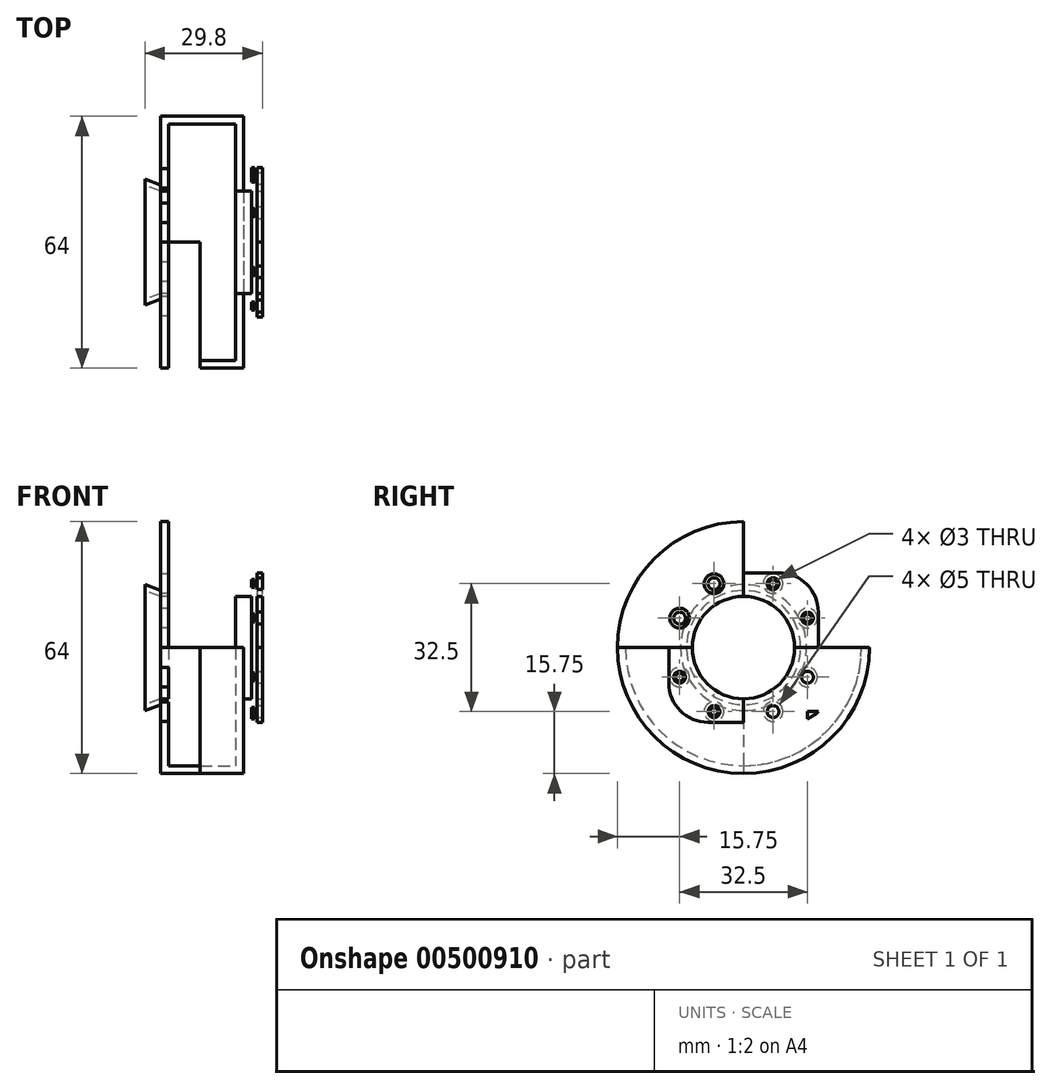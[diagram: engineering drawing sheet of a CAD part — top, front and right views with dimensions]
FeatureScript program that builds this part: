
annotation { "Feature Type Name" : "Feature", "Feature Type Description" : "" }
export const myFeature = defineFeature(function(context is Context, id is Id, definition is map)
    precondition{}
    {
        {
            var Q0;
            Q0=qCreatedBy(makeId("Right.planeOp"),FACE);
            var sketch = newSketch(context, id + "F0", { "sketchPlane" : qUnion([Q0])});
            skLineSegment(sketch, "E0.bottom", {"start": v(19, 19) * mm, "end": v(-19, 19) * mm});
            skLineSegment(sketch, "E0.top", {"start": v(19, -19) * mm, "end": v(-19, -19) * mm});
            skLineSegment(sketch, "E0.left", {"start": v(19, 19) * mm, "end": v(19, -19) * mm});
            skLineSegment(sketch, "E0.right", {"start": v(-19, 19) * mm, "end": v(-19, -19) * mm});
            skPoint(sketch, "E0.middle", {"position": v(0, 0) * mm});
            skCircle(sketch, "E1", {"center": v(0, 0) * mm, "radius": 13 * mm});
            skSolve(sketch);
        }
        {
            var Q0;
            Q0=makeQuery(id+"F0.imprint","IMPRINT",FACE,{"disambiguationData":[TD([[makeQuery(id+"F0.imprint","IMPRINT",EDGE,{"derivedFrom":sQuery(id+"F0.wireOp",EDGE,"E0.bottom")}),1.0]])]});
            extrude(context, id + "F1", {"entities" : qUnion([Q0]), "depth" : 2.8 * mm});
        }
        {
            var Q0;
            Q0=makeQuery(id+"F1.opExtrude","CAP_FACE",FACE,{"disambiguationData":[OSD([sQuery(id+"F0.wireOp",EDGE,"E0.bottom"),sQuery(id+"F0.wireOp",EDGE,"E0.top"),sQuery(id+"F0.wireOp",EDGE,"E0.left"),sQuery(id+"F0.wireOp",EDGE,"E0.right"),sQuery(id+"F0.wireOp",EDGE,"E1")])],"isStart":false});
            var sketch = newSketch(context, id + "F2", { "sketchPlane" : qUnion([Q0])});
            skLineSegment(sketch, "E2", {"start": v(-19, -19) * mm, "end": v(-16.25, -19) * mm});
            skLineSegment(sketch, "E3", {"start": v(-16.25, -19) * mm, "end": v(-16.25, -7.5) * mm});
            skCircle(sketch, "E4", {"center": v(-16.25, -7.5) * mm, "radius": 1.5 * mm});
            skLineSegment(sketch, "E5", {"start": v(-32.62, 0) * mm, "end": v(36.48, 0) * mm});
            skLineSegment(sketch, "E6", {"start": v(0, -24.37) * mm, "end": v(0, 22.32) * mm});
            skPoint(sketch, "E6.endSnap0", {"position": v(0, 19) * mm});
            skCircle(sketch, "E7.MirrorC", {"center": v(16.25, -7.5) * mm, "radius": 1.5 * mm});
            skCircle(sketch, "E8.MirrorC", {"center": v(-16.25, 7.5) * mm, "radius": 1.5 * mm});
            skCircle(sketch, "E9.MirrorC", {"center": v(16.25, 7.5) * mm, "radius": 1.5 * mm});
            skLineSegment(sketch, "E10", {"start": v(-19, -19) * mm, "end": v(-19, -16.25) * mm});
            skLineSegment(sketch, "E11", {"start": v(-19, -16.25) * mm, "end": v(-7.5, -16.25) * mm});
            skCircle(sketch, "E12", {"center": v(-7.5, -16.25) * mm, "radius": 1.5 * mm});
            skCircle(sketch, "E13.MirrorC", {"center": v(7.5, -16.25) * mm, "radius": 1.5 * mm});
            skCircle(sketch, "E14.MirrorC", {"center": v(-7.5, 16.25) * mm, "radius": 1.5 * mm});
            skCircle(sketch, "E15.MirrorC", {"center": v(7.5, 16.25) * mm, "radius": 1.5 * mm});
            skSolve(sketch);
        }
        {
            var Q0;
            Q0=makeQuery(id+"F2.imprint","IMPRINT",FACE,{"disambiguationData":[TD([[makeQuery(id+"F2.imprint","IMPRINT",EDGE,{"derivedFrom":sQuery(id+"F2.wireOp",EDGE,"E7.MirrorC")}),-1.0]])]});
            var Q1;
            Q1=makeQuery(id+"F2.imprint","IMPRINT",FACE,{"disambiguationData":[TD([[makeQuery(id+"F2.imprint","IMPRINT",EDGE,{"derivedFrom":sQuery(id+"F2.wireOp",EDGE,"E4")}),1.0]])]});
            var Q2;
            Q2=makeQuery(id+"F2.imprint","IMPRINT",FACE,{"disambiguationData":[TD([[makeQuery(id+"F2.imprint","IMPRINT",EDGE,{"derivedFrom":sQuery(id+"F2.wireOp",EDGE,"E9.MirrorC")}),1.0]])]});
            var Q3;
            Q3=makeQuery(id+"F2.imprint","IMPRINT",FACE,{"disambiguationData":[TD([[makeQuery(id+"F2.imprint","IMPRINT",EDGE,{"derivedFrom":sQuery(id+"F2.wireOp",EDGE,"E12")}),1.0]])]});
            var Q4;
            Q4=makeQuery(id+"F2.imprint","IMPRINT",FACE,{"disambiguationData":[TD([[makeQuery(id+"F2.imprint","IMPRINT",EDGE,{"derivedFrom":sQuery(id+"F2.wireOp",EDGE,"E13.MirrorC")}),-1.0]])]});
            var Q5;
            Q5=makeQuery(id+"F2.imprint","IMPRINT",FACE,{"disambiguationData":[TD([[makeQuery(id+"F2.imprint","IMPRINT",EDGE,{"derivedFrom":sQuery(id+"F2.wireOp",EDGE,"E15.MirrorC")}),1.0]])]});
            var Q6;
            Q6=makeQuery(id+"F2.imprint","IMPRINT",FACE,{"disambiguationData":[TD([[makeQuery(id+"F2.imprint","IMPRINT",EDGE,{"derivedFrom":sQuery(id+"F2.wireOp",EDGE,"E8.MirrorC")}),-1.0]])]});
            var Q7;
            Q7=makeQuery(id+"F2.imprint","IMPRINT",FACE,{"disambiguationData":[TD([[makeQuery(id+"F2.imprint","IMPRINT",EDGE,{"derivedFrom":sQuery(id+"F2.wireOp",EDGE,"E14.MirrorC")}),-1.0]])]});
            extrude(context, id + "F3", {"entities" : qUnion([Q0, Q1, Q2, Q3, Q4, Q5, Q6, Q7]), "operationType" : NewBodyOperationType.REMOVE, "oppositeDirection" : true, "depth" : 2 * mm});
        }
        {
            var Q0;
            Q0=makeQuery(id+"F1.opExtrude","CAP_FACE",FACE,{"disambiguationData":[OSD([sQuery(id+"F0.wireOp",EDGE,"E0.bottom"),sQuery(id+"F0.wireOp",EDGE,"E0.top"),sQuery(id+"F0.wireOp",EDGE,"E0.left"),sQuery(id+"F0.wireOp",EDGE,"E0.right"),sQuery(id+"F0.wireOp",EDGE,"E1")])],"isStart":true});
            var sketch = newSketch(context, id + "F4", { "sketchPlane" : qUnion([Q0])});
            skLineSegment(sketch, "E16", {"start": v(-19, -19) * mm, "end": v(-16.25, -19) * mm});
            skLineSegment(sketch, "E17", {"start": v(-16.25, -19) * mm, "end": v(-16.25, -7.5) * mm});
            skLineSegment(sketch, "E18", {"start": v(-19, -19) * mm, "end": v(-19, -16.25) * mm});
            skLineSegment(sketch, "E19", {"start": v(-19, -16.25) * mm, "end": v(-7.5, -16.25) * mm});
            skCircle(sketch, "E20", {"center": v(-16.25, -7.5) * mm, "radius": 1 * mm});
            skCircle(sketch, "E21", {"center": v(-7.5, -16.25) * mm, "radius": 1 * mm});
            skCircle(sketch, "E22.MirrorC", {"center": v(-16.25, 7.5) * mm, "radius": 1 * mm});
            skCircle(sketch, "E23.MirrorC", {"center": v(-7.5, 16.25) * mm, "radius": 1 * mm});
            skCircle(sketch, "E24.MirrorC", {"center": v(7.5, 16.25) * mm, "radius": 1 * mm});
            skCircle(sketch, "E25.MirrorC", {"center": v(7.5, -16.25) * mm, "radius": 1 * mm});
            skCircle(sketch, "E26.MirrorC", {"center": v(16.25, -7.5) * mm, "radius": 1 * mm});
            skCircle(sketch, "E27.MirrorC", {"center": v(16.25, 7.5) * mm, "radius": 1 * mm});
            skSolve(sketch);
        }
        {
            var Q0;
            Q0=makeQuery(id+"F4.imprint","IMPRINT",FACE,{"disambiguationData":[TD([[makeQuery(id+"F4.imprint","IMPRINT",EDGE,{"derivedFrom":sQuery(id+"F4.wireOp",EDGE,"E20")}),1.0]])]});
            var Q1;
            Q1=makeQuery(id+"F4.imprint","IMPRINT",FACE,{"disambiguationData":[TD([[makeQuery(id+"F4.imprint","IMPRINT",EDGE,{"derivedFrom":sQuery(id+"F4.wireOp",EDGE,"E21")}),1.0]])]});
            var Q2;
            Q2=makeQuery(id+"F4.imprint","IMPRINT",FACE,{"disambiguationData":[TD([[makeQuery(id+"F4.imprint","IMPRINT",EDGE,{"derivedFrom":sQuery(id+"F4.wireOp",EDGE,"E22.MirrorC")}),-1.0]])]});
            var Q3;
            Q3=makeQuery(id+"F4.imprint","IMPRINT",FACE,{"disambiguationData":[TD([[makeQuery(id+"F4.imprint","IMPRINT",EDGE,{"derivedFrom":sQuery(id+"F4.wireOp",EDGE,"E23.MirrorC")}),-1.0]])]});
            var Q4;
            Q4=makeQuery(id+"F4.imprint","IMPRINT",FACE,{"disambiguationData":[TD([[makeQuery(id+"F4.imprint","IMPRINT",EDGE,{"derivedFrom":sQuery(id+"F4.wireOp",EDGE,"E24.MirrorC")}),1.0]])]});
            var Q5;
            Q5=makeQuery(id+"F4.imprint","IMPRINT",FACE,{"disambiguationData":[TD([[makeQuery(id+"F4.imprint","IMPRINT",EDGE,{"derivedFrom":sQuery(id+"F4.wireOp",EDGE,"E25.MirrorC")}),-1.0]])]});
            var Q6;
            Q6=makeQuery(id+"F4.imprint","IMPRINT",FACE,{"disambiguationData":[TD([[makeQuery(id+"F4.imprint","IMPRINT",EDGE,{"derivedFrom":sQuery(id+"F4.wireOp",EDGE,"E26.MirrorC")}),-1.0]])]});
            var Q7;
            Q7=makeQuery(id+"F4.imprint","IMPRINT",FACE,{"disambiguationData":[TD([[makeQuery(id+"F4.imprint","IMPRINT",EDGE,{"derivedFrom":sQuery(id+"F4.wireOp",EDGE,"E27.MirrorC")}),1.0]])]});
            extrude(context, id + "F5", {"entities" : qUnion([Q0, Q1, Q2, Q3, Q4, Q5, Q6, Q7]), "operationType" : NewBodyOperationType.REMOVE, "oppositeDirection" : true, "depth" : 1.5 * mm});
        }
        {
            var Q0;
            Q0=makeQuery(id+"F1.opExtrude","CAP_FACE",FACE,{"disambiguationData":[OSD([sQuery(id+"F0.wireOp",EDGE,"E0.bottom"),sQuery(id+"F0.wireOp",EDGE,"E0.top"),sQuery(id+"F0.wireOp",EDGE,"E0.left"),sQuery(id+"F0.wireOp",EDGE,"E0.right"),sQuery(id+"F0.wireOp",EDGE,"E1")])],"isStart":true});
            var sketch = newSketch(context, id + "F6", { "sketchPlane" : qUnion([Q0])});
            skCircle(sketch, "E28", {"center": v(0, 0) * mm, "radius": 13 * mm});
            skCircle(sketch, "E29", {"center": v(0, 0) * mm, "radius": 14.5 * mm});
            skSolve(sketch);
        }
        {
            var Q0;
            Q0=makeQuery(id+"F6.imprint","IMPRINT",FACE,{"disambiguationData":[TD([[makeQuery(id+"F6.imprint","IMPRINT",EDGE,{"derivedFrom":sQuery(id+"F6.wireOp",EDGE,"E28")}),1.0]])]});
            extrude(context, id + "F7", {"entities" : qUnion([Q0]), "operationType" : NewBodyOperationType.ADD, "depth" : 2 * mm});
        }
        {
            var Q0;
            Q0=makeQuery(id+"F7.opExtrude","CAP_FACE",FACE,{"disambiguationData":[OSD([sQuery(id+"F6.wireOp",EDGE,"E28"),sQuery(id+"F6.wireOp",EDGE,"E29")])],"isStart":false});
            var sketch = newSketch(context, id + "F8", { "sketchPlane" : qUnion([Q0])});
            skArc(sketch, "E30", {"start": v(-32, 0) * mm, "mid": v(0, -32) * mm, "end": v(32, 0) * mm});
            skLineSegment(sketch, "E31", {"start": v(13, 0) * mm, "end": v(32, 0) * mm});
            skLineSegment(sketch, "E32", {"start": v(32, 0) * mm, "end": v(13, 0) * mm});
            skArc(sketch, "E33", {"start": v(-13, 0) * mm, "mid": v(0, -13) * mm, "end": v(13, 0) * mm});
            skLineSegment(sketch, "E34.trimOffspring", {"start": v(-13, 0) * mm, "end": v(-32, 0) * mm});
            skSolve(sketch);
        }
        {
            var Q0;
            {var subQ0=sQuery(id+"F8.wireOp",EDGE,"E33");Q0=makeQuery(id+"F8.imprint","IMPRINT",FACE,{"disambiguationData":[TD([[makeQuery(id+"F8.imprint","IMPRINT",EDGE,{"derivedFrom":subQ0}),1.0]])]});}
            var Q1;
            {var subQ0=sQuery(id+"F8.wireOp",EDGE,"E30");Q1=makeQuery(id+"F8.imprint","IMPRINT",FACE,{"disambiguationData":[TD([[makeQuery(id+"F8.imprint","IMPRINT",EDGE,{"derivedFrom":subQ0}),1.0]])]});}
            extrude(context, id + "F9", {"entities" : qUnion([Q0, Q1]), "operationType" : NewBodyOperationType.ADD, "depth" : 2 * mm});
        }
        {
            var Q0;
            Q0=makeQuery(id+"F9.opExtrude","CAP_FACE",FACE,{"disambiguationData":[OSD([sQuery(id+"F8.wireOp",EDGE,"E30"),sQuery(id+"F8.wireOp",EDGE,"E32"),sQuery(id+"F8.wireOp",EDGE,"E33"),sQuery(id+"F8.wireOp",EDGE,"E34.trimOffspring")])],"isStart":false});
            var sketch = newSketch(context, id + "F10", { "sketchPlane" : qUnion([Q0])});
            skArc(sketch, "E35", {"start": v(-32, 0) * mm, "mid": v(0, -32) * mm, "end": v(32, 0) * mm});
            skArc(sketch, "E36", {"start": v(-30, 0) * mm, "mid": v(0, -30) * mm, "end": v(30, 0) * mm});
            skLineSegment(sketch, "E37", {"start": v(0, 0) * mm, "end": v(-32, 0) * mm});
            skLineSegment(sketch, "E38", {"start": v(-32, 0) * mm, "end": v(32, 0) * mm});
            skSolve(sketch);
        }
        {
            var Q0;
            {var subQ0=sQuery(id+"F10.wireOp",EDGE,"E35");Q0=makeQuery(id+"F10.imprint","IMPRINT",FACE,{"disambiguationData":[TD([[makeQuery(id+"F10.imprint","IMPRINT",EDGE,{"derivedFrom":subQ0}),1.0]])]});}
            extrude(context, id + "F11", {"entities" : qUnion([Q0]), "operationType" : NewBodyOperationType.ADD, "depth" : 17 * mm});
        }
        {
            var Q0;
            Q0=makeQuery(id+"F11.opExtrude","CAP_FACE",FACE,{"disambiguationData":[OSD([sQuery(id+"F10.wireOp",EDGE,"E35"),sQuery(id+"F10.wireOp",EDGE,"E36"),sQuery(id+"F10.wireOp",EDGE,"E38")])],"isStart":false});
            var sketch = newSketch(context, id + "F12", { "sketchPlane" : qUnion([Q0])});
            skCircle(sketch, "E39", {"center": v(0, 0) * mm, "radius": 32 * mm});
            skCircle(sketch, "E40", {"center": v(0, 0) * mm, "radius": 13 * mm});
            skSolve(sketch);
        }
        {
            var Q0;
            Q0 = qSketchRegion(id + "F12", true);
            extrude(context, id + "F13", {"entities" : qUnion([Q0]), "operationType" : NewBodyOperationType.ADD, "depth" : 2 * mm});
        }
        {
            var Q0;
            Q0=makeQuery(id+"F13.opExtrude","CAP_FACE",FACE,{"disambiguationData":[OSD([sQuery(id+"F12.wireOp",EDGE,"E39"),sQuery(id+"F12.wireOp",EDGE,"E40")])],"isStart":false});
            var sketch = newSketch(context, id + "F14", { "sketchPlane" : qUnion([Q0])});
            skLineSegment(sketch, "E41", {"start": v(0, 0) * mm, "end": v(-19, 0) * mm});
            skLineSegment(sketch, "E42", {"start": v(-19, 0) * mm, "end": v(-19, -19) * mm});
            skLineSegment(sketch, "E43", {"start": v(-19, -19) * mm, "end": v(-16.25, -19) * mm});
            skLineSegment(sketch, "E44", {"start": v(-16.25, -19) * mm, "end": v(-16.25, -7.5) * mm});
            skLineSegment(sketch, "E45", {"start": v(-19, -19) * mm, "end": v(-19, -16.25) * mm});
            skLineSegment(sketch, "E46", {"start": v(-19, -16.25) * mm, "end": v(-7.5, -16.25) * mm});
            skLineSegment(sketch, "E47", {"start": v(0, 0) * mm, "end": v(0, 35.4) * mm});
            skLineSegment(sketch, "E48", {"start": v(0, 35.4) * mm, "end": v(0, -36.23) * mm});
            skLineSegment(sketch, "E49", {"start": v(0, 0) * mm, "end": v(39.08, 0) * mm});
            skLineSegment(sketch, "E50", {"start": v(39.08, 0) * mm, "end": v(-45.88, 0) * mm});
            skCircle(sketch, "E51", {"center": v(-7.5, -16.25) * mm, "radius": 2.5 * mm});
            skCircle(sketch, "E52", {"center": v(-16.25, -7.5) * mm, "radius": 2.5 * mm});
            skCircle(sketch, "E53.MirrorC", {"center": v(7.5, -16.25) * mm, "radius": 2.5 * mm});
            skCircle(sketch, "E54.MirrorC", {"center": v(16.25, -7.5) * mm, "radius": 2.5 * mm});
            skCircle(sketch, "E55.MirrorC", {"center": v(-16.25, 7.5) * mm, "radius": 2.5 * mm});
            skCircle(sketch, "E56.MirrorC", {"center": v(16.25, 7.5) * mm, "radius": 2.5 * mm});
            skCircle(sketch, "E57.MirrorC", {"center": v(7.5, 16.25) * mm, "radius": 2.5 * mm});
            skCircle(sketch, "E58.MirrorC", {"center": v(-7.5, 16.25) * mm, "radius": 2.5 * mm});
            skSolve(sketch);
        }
        {
            var Q0;
            Q0=makeQuery(id+"F14.imprint","IMPRINT",FACE,{"disambiguationData":[TD([[makeQuery(id+"F14.imprint","IMPRINT",EDGE,{"derivedFrom":sQuery(id+"F14.wireOp",EDGE,"E51")}),1.0]])]});
            var Q1;
            Q1=makeQuery(id+"F14.imprint","IMPRINT",FACE,{"disambiguationData":[TD([[makeQuery(id+"F14.imprint","IMPRINT",EDGE,{"derivedFrom":sQuery(id+"F14.wireOp",EDGE,"E52")}),1.0]])]});
            var Q2;
            Q2=makeQuery(id+"F14.imprint","IMPRINT",FACE,{"disambiguationData":[TD([[makeQuery(id+"F14.imprint","IMPRINT",EDGE,{"derivedFrom":sQuery(id+"F14.wireOp",EDGE,"E53.MirrorC")}),-1.0]])]});
            var Q3;
            Q3=makeQuery(id+"F14.imprint","IMPRINT",FACE,{"disambiguationData":[TD([[makeQuery(id+"F14.imprint","IMPRINT",EDGE,{"derivedFrom":sQuery(id+"F14.wireOp",EDGE,"E54.MirrorC")}),-1.0]])]});
            var Q4;
            Q4=makeQuery(id+"F14.imprint","IMPRINT",FACE,{"disambiguationData":[TD([[makeQuery(id+"F14.imprint","IMPRINT",EDGE,{"derivedFrom":sQuery(id+"F14.wireOp",EDGE,"E55.MirrorC")}),-1.0]])]});
            var Q5;
            Q5=makeQuery(id+"F14.imprint","IMPRINT",FACE,{"disambiguationData":[TD([[makeQuery(id+"F14.imprint","IMPRINT",EDGE,{"derivedFrom":sQuery(id+"F14.wireOp",EDGE,"E56.MirrorC")}),1.0]])]});
            var Q6;
            Q6=makeQuery(id+"F14.imprint","IMPRINT",FACE,{"disambiguationData":[TD([[makeQuery(id+"F14.imprint","IMPRINT",EDGE,{"derivedFrom":sQuery(id+"F14.wireOp",EDGE,"E57.MirrorC")}),1.0]])]});
            var Q7;
            Q7=makeQuery(id+"F14.imprint","IMPRINT",FACE,{"disambiguationData":[TD([[makeQuery(id+"F14.imprint","IMPRINT",EDGE,{"derivedFrom":sQuery(id+"F14.wireOp",EDGE,"E58.MirrorC")}),-1.0]])]});
            extrude(context, id + "F15", {"entities" : qUnion([Q0, Q1, Q2, Q3, Q4, Q5, Q6, Q7]), "operationType" : NewBodyOperationType.REMOVE, "oppositeDirection" : true, "depth" : 10 * mm});
        }
        {
            var Q0;
            Q0=qCreatedBy(makeId("Front.planeOp"),FACE);
            var sketch = newSketch(context, id + "F16", { "sketchPlane" : qUnion([Q0])});
            skLineSegment(sketch, "E59", {"start": v(0, 0) * mm, "end": v(-23, 0) * mm});
            skLineSegment(sketch, "E60", {"start": v(-23, 0) * mm, "end": v(-23, -13) * mm});
            skLineSegment(sketch, "E61", {"start": v(-23, -13) * mm, "end": v(-23, -14.5) * mm});
            skLineSegment(sketch, "E62", {"start": v(-27, -14.5) * mm, "end": v(-27, -16) * mm});
            skLineSegment(sketch, "E63", {"start": v(-27, -16) * mm, "end": v(-23, -14.5) * mm});
            skLineSegment(sketch, "E64", {"start": v(-27, -14.5) * mm, "end": v(-23, -13) * mm});
            skLineSegment(sketch, "E65", {"start": v(0, 0) * mm, "end": v(-28.02, 0) * mm});
            skSolve(sketch);
        }
        {
            var Q0;
            Q0=makeQuery(id+"F16.imprint","IMPRINT",FACE,{"disambiguationData":[TD([[makeQuery(id+"F16.imprint","IMPRINT",EDGE,{"derivedFrom":sQuery(id+"F16.wireOp",EDGE,"E61")}),-1.0]])]});
            var Q1;
            Q1=sQuery(id+"F16.wireOp",EDGE,"E65");
            revolve(context, id + "F17", {"entities" : qUnion([Q0]), "axis" : qUnion([Q1]), "revolveType" : RevolveType.FULL});
        }
        {
            var Q0;
            Q0=makeQuery(id+"F1.opExtrude","SWEPT_EDGE",EDGE,{"disambiguationData":[OSD([sQuery(id+"F0.wireOp",EDGE,"E0.bottom"),sQuery(id+"F0.wireOp",EDGE,"E0.left")])]});
            var Q1;
            Q1=makeQuery(id+"F1.opExtrude","SWEPT_EDGE",EDGE,{"disambiguationData":[OSD([sQuery(id+"F0.wireOp",EDGE,"E0.top"),sQuery(id+"F0.wireOp",EDGE,"E0.left")])]});
            var Q2;
            Q2=makeQuery(id+"F1.opExtrude","SWEPT_EDGE",EDGE,{"disambiguationData":[OSD([sQuery(id+"F0.wireOp",EDGE,"E0.top"),sQuery(id+"F0.wireOp",EDGE,"E0.right")])]});
            var Q3;
            Q3=makeQuery(id+"F1.opExtrude","SWEPT_EDGE",EDGE,{"disambiguationData":[OSD([sQuery(id+"F0.wireOp",EDGE,"E0.bottom"),sQuery(id+"F0.wireOp",EDGE,"E0.right")])]});
            fillet(context, id + "F18", {"entities" : qUnion([Q0, Q1, Q2, Q3]), "radius" : 10 * mm, "tangentPropagation" : true, "allowEdgeOverflow" : false});
        }
    });
